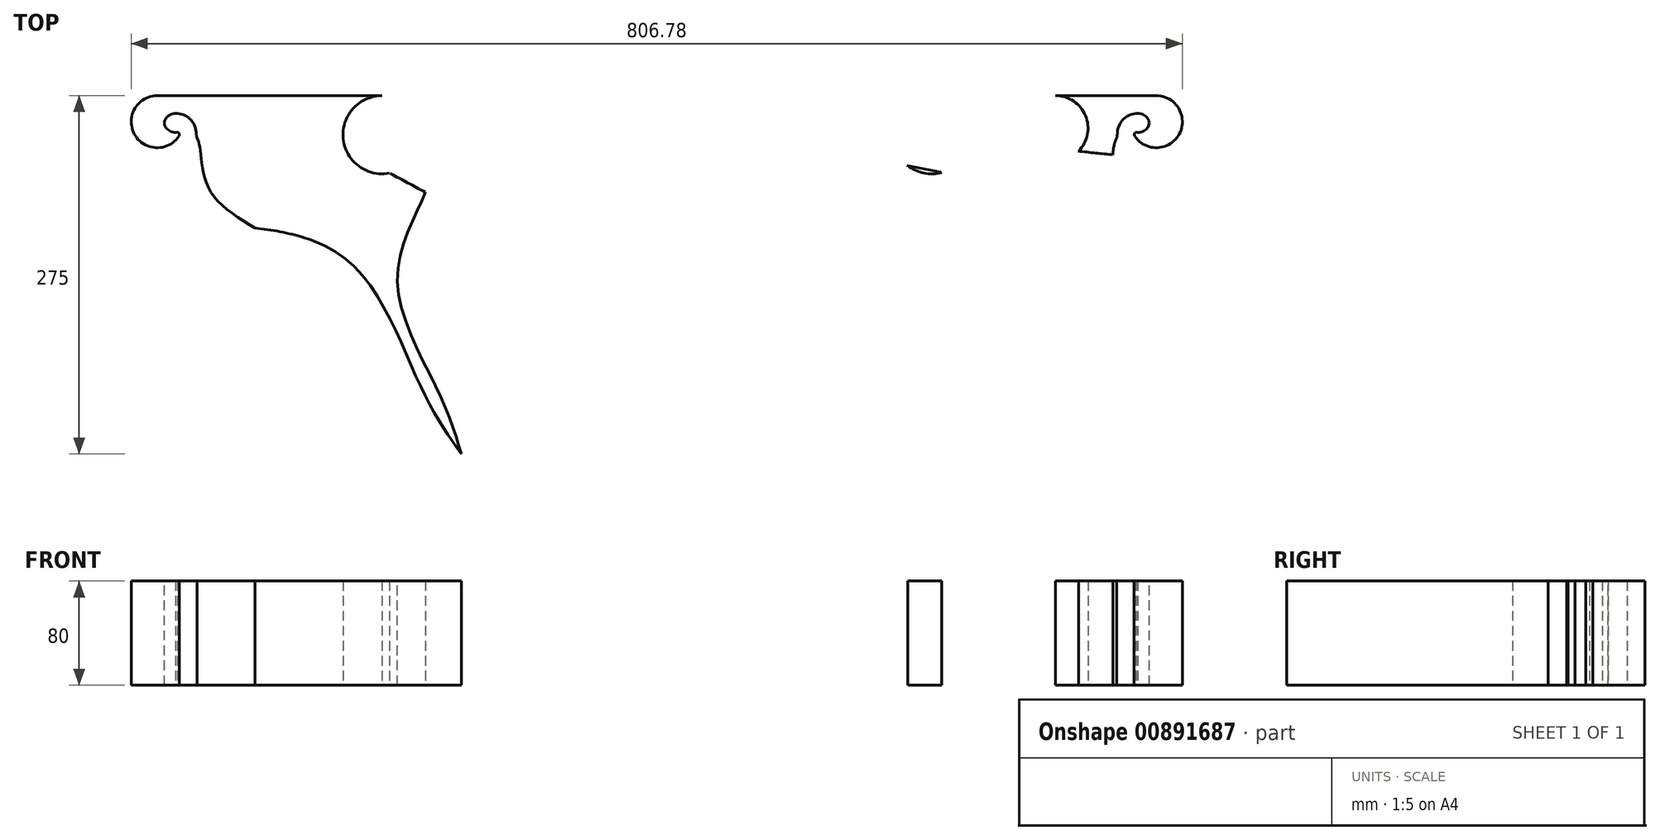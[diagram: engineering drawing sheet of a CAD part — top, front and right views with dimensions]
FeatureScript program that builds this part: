
annotation { "Feature Type Name" : "Feature", "Feature Type Description" : "" }
export const myFeature = defineFeature(function(context is Context, id is Id, definition is map)
    precondition{}
    {
        {
            var Q0;
            Q0=qCreatedBy(makeId("Top.planeOp"),FACE);
            var sketch = newSketch(context, id + "F0", { "sketchPlane" : qUnion([Q0])});
            skFitSpline(sketch, "E0.0.0", {"points": [v(222.24, 427.22) * mm, v(215.5, 429.07) * mm, v(196.44, 434.28) * mm, v(159.63, 464.69) * mm, v(135.76, 484.28) * mm]});
            skArc(sketch, "E0.0.1", {"start": v(135.76, 484.28) * mm, "mid": v(0, 567.46) * mm, "end": v(-135.76, 484.28) * mm});
            skFitSpline(sketch, "E0.0.2", {"points": [v(-135.76, 484.28) * mm, v(-159.63, 464.69) * mm, v(-196.44, 434.28) * mm, v(-215.5, 429.07) * mm, v(-222.24, 427.22) * mm]});
            skArc(sketch, "E0.0.4", {"start": v(-309.42, 390.28) * mm, "mid": v(-312.68, 382.2) * mm, "end": v(-319.87, 377.3) * mm});
            skFitSpline(sketch, "E0.0.5", {"points": [v(-314.05, 379.09) * mm, v(-349.26, 368.46) * mm, v(-392.1, 351.55) * mm, v(-410.06, 337.43) * mm]});
            skEllipticalArc(sketch, "E0.0.6", {});
            skArc(sketch, "E0.0.7", {"start": v(-404.46, 196.44) * mm, "mid": v(-395.87, 191.21) * mm, "end": v(-386.4, 187.8) * mm});
            skFitSpline(sketch, "E0.0.8", {"points": [v(-394.78, 189.9) * mm, v(-344.92, 177.5) * mm, v(-241.75, 151.88) * mm, v(-181.26, 51.75) * mm, v(-150, 0) * mm]});
            skLineSegment(sketch, "E0.0.9", {"start": v(-150, 0) * mm, "end": v(-90, 0) * mm});
            skLineSegment(sketch, "E0.0.10", {"start": v(-90, 0) * mm, "end": v(-90, 110) * mm});
            skArc(sketch, "E0.0.11", {"start": v(-90, 110) * mm, "mid": v(0, 200) * mm, "end": v(90, 110) * mm});
            skLineSegment(sketch, "E0.0.12", {"start": v(90, 110) * mm, "end": v(90, 0) * mm});
            skLineSegment(sketch, "E0.0.13", {"start": v(90, 0) * mm, "end": v(150, 0) * mm});
            skFitSpline(sketch, "E0.0.14", {"points": [v(150, 0) * mm, v(181.26, 51.75) * mm, v(241.75, 151.88) * mm, v(344.92, 177.5) * mm, v(394.78, 189.9) * mm]});
            skArc(sketch, "E0.0.15", {"start": v(386.4, 187.8) * mm, "mid": v(395.87, 191.21) * mm, "end": v(404.46, 196.44) * mm});
            skEllipticalArc(sketch, "E0.0.16", {});
            skFitSpline(sketch, "E0.0.17", {"points": [v(410.06, 337.43) * mm, v(392.1, 351.55) * mm, v(349.26, 368.46) * mm, v(314.05, 379.09) * mm]});
            skLineSegment(sketch, "E1.0", {"start": v(-240.1, 290) * mm, "end": v(-178.5, 290) * mm});
            skLineSegment(sketch, "E1.1", {"start": v(-178.5, 290) * mm, "end": v(-178.5, 325.2) * mm});
            skLineSegment(sketch, "E1.2", {"start": v(-178.5, 325.2) * mm, "end": v(-240.1, 325.2) * mm});
            skLineSegment(sketch, "E1.3", {"start": v(-240.1, 290) * mm, "end": v(-240.1, 325.2) * mm});
            skLineSegment(sketch, "E1.4", {"start": v(-250.1, 290) * mm, "end": v(-250.1, 325.2) * mm});
            skLineSegment(sketch, "E1.5", {"start": v(-250.1, 325.2) * mm, "end": v(-311.7, 325.2) * mm});
            skLineSegment(sketch, "E1.6", {"start": v(-311.7, 290) * mm, "end": v(-250.1, 290) * mm});
            skLineSegment(sketch, "E1.7", {"start": v(-311.7, 290) * mm, "end": v(-311.7, 325.2) * mm});
            skLineSegment(sketch, "E2.0", {"start": v(-383.3, 290) * mm, "end": v(-321.7, 290) * mm});
            skLineSegment(sketch, "E3.0", {"start": v(-321.7, 325.2) * mm, "end": v(-383.3, 325.2) * mm});
            skLineSegment(sketch, "E4.0", {"start": v(-321.7, 290) * mm, "end": v(-321.7, 325.2) * mm});
            skLineSegment(sketch, "E5.0", {"start": v(-383.3, 290) * mm, "end": v(-383.3, 325.2) * mm});
            skFitSpline(sketch, "E6.0", {"points": [v(-342.67, 339.28) * mm, v(-317.97, 353.62) * mm, v(-277.69, 364.45) * mm, v(-252.88, 405.7) * mm, v(-252.65, 405.6) * mm, v(-252.66, 408.6) * mm]});
            skArc(sketch, "E7.0", {"start": v(-250.27, 406.87) * mm, "mid": v(-251.77, 407.17) * mm, "end": v(-252.75, 406) * mm});
            skFitSpline(sketch, "E8.0", {"points": [v(-250.27, 406.87) * mm, v(-244.43, 403.08) * mm, v(-228.6, 392.87) * mm, v(-192.33, 407.72) * mm, v(-169.18, 417.08) * mm]});
            skArc(sketch, "E9.0", {"start": v(-169.05, 414.28) * mm, "mid": v(-169.97, 415.86) * mm, "end": v(-171.8, 416.02) * mm});
            skArc(sketch, "E10.0", {"start": v(-332.8, 344.66) * mm, "mid": v(-334, 342.02) * mm, "end": v(-331.71, 340.22) * mm});
            skArc(sketch, "E11.0.0", {"start": v(367.9, 246.89) * mm, "mid": v(366.57, 245.65) * mm, "end": v(366.79, 243.85) * mm});
            skArc(sketch, "E11.0.1", {"start": v(366.79, 243.85) * mm, "mid": v(401.04, 245.6) * mm, "end": v(383.39, 275) * mm});
            skLineSegment(sketch, "E11.0.2", {"start": v(383.39, 275) * mm, "end": v(-383.39, 275) * mm});
            skArc(sketch, "E11.0.3", {"start": v(-383.39, 275) * mm, "mid": v(-401.04, 245.6) * mm, "end": v(-366.79, 243.85) * mm});
            skArc(sketch, "E11.0.4", {"start": v(-366.79, 243.85) * mm, "mid": v(-366.57, 245.65) * mm, "end": v(-367.9, 246.89) * mm});
            skEllipticalArc(sketch, "E11.0.5", {});
            skArc(sketch, "E11.0.6", {"start": v(-369.23, 261.25) * mm, "mid": v(-358.46, 257.25) * mm, "end": v(-353.55, 246.86) * mm});
            skArc(sketch, "E11.0.7", {"start": v(-353.55, 246.86) * mm, "mid": v(-353.08, 242.95) * mm, "end": v(-352.1, 239.13) * mm});
            skFitSpline(sketch, "E11.0.8", {"points": [v(-353.7, 243.85) * mm, v(-350.61, 235.19) * mm, v(-342.3, 200.93) * mm, v(-287.54, 161.27) * mm, v(-255.18, 135.34) * mm]});
            skFitSpline(sketch, "E11.0.9", {"points": [v(-394.78, 189.9) * mm, v(-344.92, 177.5) * mm, v(-241.75, 151.88) * mm, v(-181.26, 51.75) * mm, v(-150, 0) * mm]});
            skFitSpline(sketch, "E11.0.15", {"points": [v(150, 0) * mm, v(181.26, 51.75) * mm, v(241.75, 151.88) * mm, v(344.92, 177.5) * mm, v(394.78, 189.9) * mm]});
            skFitSpline(sketch, "E11.0.16", {"points": [v(255.18, 135.34) * mm, v(287.54, 161.27) * mm, v(342.3, 200.93) * mm, v(350.61, 235.19) * mm, v(353.7, 243.85) * mm]});
            skArc(sketch, "E11.0.17", {"start": v(352.1, 239.13) * mm, "mid": v(353.08, 242.95) * mm, "end": v(353.55, 246.86) * mm});
            skArc(sketch, "E11.0.18", {"start": v(353.55, 246.86) * mm, "mid": v(358.46, 257.25) * mm, "end": v(369.23, 261.25) * mm});
            skEllipticalArc(sketch, "E11.0.19", {});
            skLineSegment(sketch, "E12.0.0", {"start": v(305.94, 275) * mm, "end": v(-305.94, 275) * mm});
            skArc(sketch, "E12.0.1", {"start": v(-305.94, 275) * mm, "mid": v(-327.36, 237.1) * mm, "end": v(-283.84, 238.31) * mm});
            skArc(sketch, "E12.0.2", {"start": v(-283.84, 238.31) * mm, "mid": v(-283.78, 240.06) * mm, "end": v(-285.12, 241.19) * mm});
            skEllipticalArc(sketch, "E12.0.3", {});
            skFitSpline(sketch, "E12.0.4", {"points": [v(-286.27, 259.2) * mm, v(1000, -265.74) * mm, v(256.47, 1000) * mm]});
            skFitSpline(sketch, "E12.0.5", {"points": [v(-285.63, 259.1) * mm, v(1000, -265.14) * mm, v(258.09, 1000) * mm]});
            skFitSpline(sketch, "E12.0.6", {"points": [v(-265.5, 243.26) * mm, v(-263.97, 221.32) * mm, v(-260.75, 173.86) * mm, v(-230.38, 123.02) * mm, v(-214.22, 95.6) * mm]});
            skFitSpline(sketch, "E12.0.7", {"points": [v(-394.78, 189.9) * mm, v(-344.92, 177.5) * mm, v(-241.75, 151.88) * mm, v(-181.26, 51.75) * mm, v(-150, 0) * mm]});
            skFitSpline(sketch, "E12.0.13", {"points": [v(150, 0) * mm, v(181.26, 51.75) * mm, v(241.75, 151.88) * mm, v(344.92, 177.5) * mm, v(394.78, 189.9) * mm]});
            skFitSpline(sketch, "E12.0.14", {"points": [v(214.22, 95.6) * mm, v(230.38, 123.02) * mm, v(260.75, 173.86) * mm, v(263.97, 221.32) * mm, v(265.5, 243.26) * mm]});
            skFitSpline(sketch, "E12.0.15", {"points": [v(265.14, 238.31) * mm, v(1000, 265.14) * mm, v(258.09, 1000) * mm]});
            skLineSegment(sketch, "E12.0.16", {"start": v(285.63, 259.1) * mm, "end": v(286.27, 259.2) * mm});
            skEllipticalArc(sketch, "E12.0.17", {});
            skArc(sketch, "E12.0.18", {"start": v(285.12, 241.19) * mm, "mid": v(283.78, 240.06) * mm, "end": v(283.84, 238.31) * mm});
            skArc(sketch, "E12.0.19", {"start": v(283.84, 238.31) * mm, "mid": v(327.36, 237.1) * mm, "end": v(305.94, 275) * mm});
            skArc(sketch, "E13.0.0", {"start": v(188.69, 224.82) * mm, "mid": v(238.32, 232.86) * mm, "end": v(210.88, 275) * mm});
            skLineSegment(sketch, "E13.0.1", {"start": v(210.88, 275) * mm, "end": v(-210.88, 275) * mm});
            skArc(sketch, "E13.0.2", {"start": v(-210.88, 275) * mm, "mid": v(-238.32, 232.86) * mm, "end": v(-188.69, 224.82) * mm});
            skArc(sketch, "E13.0.3", {"start": v(-188.69, 224.82) * mm, "mid": v(-188.58, 226.71) * mm, "end": v(-190.1, 227.85) * mm});
            skEllipticalArc(sketch, "E13.0.4", {});
            skFitSpline(sketch, "E13.0.5", {"points": [v(-190.78, 251.9) * mm, v(1000, -168.95) * mm, v(251.9, 1000) * mm]});
            skArc(sketch, "E13.0.6", {"start": v(-170.52, 233.6) * mm, "mid": v(-170.48, 227.5) * mm, "end": v(-171.67, 221.5) * mm});
            skFitSpline(sketch, "E13.0.7", {"points": [v(-170.36, 225.76) * mm, v(-179.25, 197.05) * mm, v(-199.12, 132.86) * mm, v(-167.48, 47.3) * mm, v(-150, 0) * mm]});
            skFitSpline(sketch, "E13.0.13", {"points": [v(150, 0) * mm, v(167.48, 47.3) * mm, v(199.12, 132.86) * mm, v(179.25, 197.05) * mm, v(170.36, 225.76) * mm]});
            skArc(sketch, "E13.0.14", {"start": v(171.67, 221.5) * mm, "mid": v(170.48, 227.5) * mm, "end": v(170.52, 233.6) * mm});
            skFitSpline(sketch, "E13.0.15", {"points": [v(170.36, 225.76) * mm, v(1000, 168.95) * mm, v(251.9, 1000) * mm]});
            skEllipticalArc(sketch, "E13.0.16", {});
            skArc(sketch, "E13.0.17", {"start": v(190.1, 227.85) * mm, "mid": v(188.58, 226.71) * mm, "end": v(188.69, 224.82) * mm});
            skLineSegment(sketch, "E14", {"start": v(-331.71, 340.22) * mm, "end": v(-198.5, 340.69) * mm});
            skLineSegment(sketch, "E15", {"start": v(-168.92, 340.79) * mm, "end": v(-169.05, 414.28) * mm});
            skFitSpline(sketch, "E16", {"points": [v(-309.42, 390.28) * mm, v(-310.43, 397.88) * mm, v(-313.22, 403.87) * mm, v(-319.74, 407.36) * mm, v(-326.56, 409.03) * mm, v(-336.27, 408.88) * mm, v(-344.6, 406.3) * mm, v(-349.31, 401.45) * mm, v(-350.68, 396.14) * mm, v(-348.1, 390.38) * mm, v(-342.18, 385.98) * mm, v(-349.31, 386.43) * mm, v(-357.3, 391.91) * mm, v(-359.87, 398.89) * mm, v(-360.53, 404.48) * mm, v(-359.92, 410.03) * mm, v(-358.56, 414.95) * mm, v(-355.53, 420.61) * mm, v(-347.6, 428.48) * mm, v(-336.84, 434.93) * mm, v(-325.35, 437.99) * mm, v(-316.06, 437.95) * mm, v(-306.16, 435.7) * mm, v(-299.83, 432.89) * mm, v(-292.54, 427.4) * mm, v(-289.54, 422.08) * mm, v(-289.78, 416.43) * mm, v(-288.99, 413.5) * mm, v(-284.18, 413.54) * mm, v(-277.28, 420.3) * mm, v(-275.39, 426.5) * mm, v(-275.68, 437.35) * mm, v(-274.73, 450.85) * mm, v(-268.87, 462.58) * mm, v(-258.44, 470.61) * mm, v(-245.92, 473.96) * mm, v(-234.58, 474.32) * mm, v(-224.62, 471.95) * mm, v(-219.05, 468.93) * mm, v(-214.82, 465.41) * mm, v(-210.76, 459.35) * mm, v(-210.3, 450.66) * mm, v(-213.6, 444.23) * mm, v(-219.23, 439.08) * mm, v(-223.94, 437.12) * mm, v(-226.82, 436.48) * mm, v(-228.8, 436.84) * mm, v(-227, 438.29) * mm, v(-224.93, 439.28) * mm, v(-222.76, 440.81) * mm, v(-221.4, 443.17) * mm, v(-220.7, 446.77) * mm, v(-221.12, 450.52) * mm, v(-223.7, 453.85) * mm, v(-227.55, 456.2) * mm, v(-231.66, 457.32) * mm, v(-236.43, 457.82) * mm, v(-239.68, 457.23) * mm, v(-243.44, 455.26) * mm, v(-247.03, 451.54) * mm, v(-248.96, 447.62) * mm, v(-249.62, 441.06) * mm, v(-248.82, 436.85) * mm, v(-246.6, 432.46) * mm, v(-243.05, 429.54) * mm, v(-238.25, 427.74) * mm, v(-231.93, 426.7) * mm, v(-225.96, 426.77) * mm, v(-222.24, 427.22) * mm], "startDerivative": vector(-24.65, 493.31) * mm, "endDerivative": vector(305.63, 42.31) * mm});
            skFitSpline(sketch, "E17.MirrorCS", {"points": [v(309.42, 390.28) * mm, v(310.43, 397.88) * mm, v(313.22, 403.87) * mm, v(319.74, 407.36) * mm, v(326.56, 409.03) * mm, v(336.27, 408.88) * mm, v(344.6, 406.3) * mm, v(349.31, 401.45) * mm, v(350.68, 396.14) * mm, v(348.1, 390.38) * mm, v(342.18, 385.98) * mm, v(349.31, 386.43) * mm, v(357.3, 391.91) * mm, v(359.87, 398.89) * mm, v(360.53, 404.48) * mm, v(359.92, 410.03) * mm, v(358.56, 414.95) * mm, v(355.53, 420.61) * mm, v(347.6, 428.48) * mm, v(336.84, 434.93) * mm, v(325.35, 437.99) * mm, v(316.06, 437.95) * mm, v(306.16, 435.7) * mm, v(299.83, 432.89) * mm, v(292.54, 427.4) * mm, v(289.54, 422.08) * mm, v(289.78, 416.43) * mm, v(288.99, 413.5) * mm, v(284.18, 413.54) * mm, v(277.28, 420.3) * mm, v(275.39, 426.5) * mm, v(275.68, 437.35) * mm, v(274.73, 450.85) * mm, v(268.87, 462.58) * mm, v(258.44, 470.61) * mm, v(245.92, 473.96) * mm, v(234.58, 474.32) * mm, v(224.62, 471.95) * mm, v(219.05, 468.93) * mm, v(214.82, 465.41) * mm, v(210.76, 459.35) * mm, v(210.3, 450.66) * mm, v(213.6, 444.23) * mm, v(219.23, 439.08) * mm, v(223.94, 437.12) * mm, v(226.82, 436.48) * mm, v(228.8, 436.84) * mm, v(227, 438.29) * mm, v(224.93, 439.28) * mm, v(222.76, 440.81) * mm, v(221.4, 443.17) * mm, v(220.7, 446.77) * mm, v(221.12, 450.52) * mm, v(223.7, 453.85) * mm, v(227.55, 456.2) * mm, v(231.66, 457.32) * mm, v(236.43, 457.82) * mm, v(239.68, 457.23) * mm, v(243.44, 455.26) * mm, v(247.03, 451.54) * mm, v(248.96, 447.62) * mm, v(249.62, 441.06) * mm, v(248.82, 436.85) * mm, v(246.6, 432.46) * mm, v(243.05, 429.54) * mm, v(238.25, 427.74) * mm, v(231.93, 426.7) * mm, v(225.96, 426.77) * mm, v(222.24, 427.22) * mm], "startDerivative": vector(24.65, 493.31) * mm, "endDerivative": vector(-305.63, 42.31) * mm});
            skFitSpline(sketch, "E18.MirrorCS", {"points": [v(342.67, 339.28) * mm, v(317.97, 353.62) * mm, v(277.69, 364.45) * mm, v(252.88, 405.7) * mm, v(252.65, 405.6) * mm, v(252.66, 408.6) * mm]});
            skFitSpline(sketch, "E19.MirrorCS", {"points": [v(250.27, 406.87) * mm, v(244.43, 403.08) * mm, v(228.6, 392.87) * mm, v(192.33, 407.72) * mm, v(169.18, 417.08) * mm]});
            skLineSegment(sketch, "E20.MirrorCS", {"start": v(168.92, 340.79) * mm, "end": v(169.05, 414.28) * mm});
            skLineSegment(sketch, "E21.MirrorCS", {"start": v(331.71, 340.22) * mm, "end": v(168.92, 340.79) * mm});
            skArc(sketch, "E22.MirrorCS", {"start": v(169.05, 414.28) * mm, "mid": v(169.97, 415.86) * mm, "end": v(171.8, 416.02) * mm});
            skArc(sketch, "E23.MirrorCS", {"start": v(250.27, 406.87) * mm, "mid": v(251.77, 407.17) * mm, "end": v(252.75, 406) * mm});
            skArc(sketch, "E24.MirrorCS", {"start": v(332.8, 344.66) * mm, "mid": v(334, 342.02) * mm, "end": v(331.71, 340.22) * mm});
            skArc(sketch, "E25.MirrorCS", {"start": v(309.42, 390.28) * mm, "mid": v(312.68, 382.2) * mm, "end": v(319.87, 377.3) * mm});
            skFitSpline(sketch, "E26", {"points": [v(-250.27, 406.87) * mm, v(-244.43, 403.08) * mm, v(-228.6, 392.87) * mm, v(-192.33, 407.72) * mm, v(-169.18, 417.08) * mm]});
            skLineSegment(sketch, "E27", {"start": v(-198.5, 340.69) * mm, "end": v(-168.92, 340.79) * mm});
            skPoint(sketch, "E28", {"position": v(0, 275) * mm});
            skLineSegment(sketch, "E29", {"start": v(-178.5, 340.75) * mm, "end": v(-178.5, 413.32) * mm});
            skLineSegment(sketch, "E30.MirrorCS", {"start": v(178.5, 340.75) * mm, "end": v(178.5, 413.32) * mm});
            skLineSegment(sketch, "E31.MirrorCS", {"start": v(178.5, 290) * mm, "end": v(178.5, 325.2) * mm});
            skLineSegment(sketch, "E32.MirrorCS", {"start": v(178.5, 325.2) * mm, "end": v(240.1, 325.2) * mm});
            skLineSegment(sketch, "E33.MirrorCS", {"start": v(240.1, 290) * mm, "end": v(178.5, 290) * mm});
            skLineSegment(sketch, "E34.MirrorCS", {"start": v(240.1, 290) * mm, "end": v(240.1, 325.2) * mm});
            skLineSegment(sketch, "E35.MirrorCS", {"start": v(250.1, 290) * mm, "end": v(250.1, 325.2) * mm});
            skLineSegment(sketch, "E36.MirrorCS", {"start": v(250.1, 325.2) * mm, "end": v(311.7, 325.2) * mm});
            skLineSegment(sketch, "E37.MirrorCS", {"start": v(311.7, 290) * mm, "end": v(250.1, 290) * mm});
            skLineSegment(sketch, "E38.MirrorCS", {"start": v(311.7, 290) * mm, "end": v(311.7, 325.2) * mm});
            skLineSegment(sketch, "E39.MirrorCS", {"start": v(321.7, 290) * mm, "end": v(321.7, 325.2) * mm});
            skLineSegment(sketch, "E40.MirrorCS", {"start": v(321.7, 325.2) * mm, "end": v(383.3, 325.2) * mm});
            skLineSegment(sketch, "E41.MirrorCS", {"start": v(383.3, 290) * mm, "end": v(321.7, 290) * mm});
            skLineSegment(sketch, "E42.MirrorCS", {"start": v(383.3, 290) * mm, "end": v(383.3, 325.2) * mm});
            const initialGuessF0  = {"E0.0.6": [-0.34931216680627963, 0.26310522471521947, -0.8795186508433591, 0.4758644164241295, 0.09801349999999999, 0.086147, 5.8461119226871325, 1.3987543209554119], "E0.0.16": [0.34931216680627963, 0.26310522471521947, 0.8795186508433591, 0.4758644164241295, 0.09801349999999999, 0.086147, 4.884430986224174, 0.4370733844924535], "E11.0.5": [-0.3692299729374505, 0.25402610760164496, -1, 0, 0.00868, 0.0072229875998473525, 4.71238898038469, 1.7242785659408997], "E11.0.19": [0.3692299729374472, 0.2540261076016343, 1, 0, 0.00868, 0.0072229875998473525, 4.558906741237017, 1.5707963267948966], "E12.0.3": [-0.2862692176634982, 0.25016623719894915, 1, 0, 0.01114790895395411, 0.00902888915716235, 1.5707963267948966, 4.816091749526819], "E12.0.17": [0.28626921761494883, 0.25016623719894915, 1, 0, 0.01114790895395411, 0.00902888915716235, 4.6086862112438105, 1.5707963267948968], "E13.0.4": [-0.19077662931411604, 0.2398668370838165, -1, 0, 0.012873693325351057, 0.012037203490749382, 4.71238898038469, 1.6233236227230905], "E13.0.16": [0.19077662931381673, 0.2398668370838165, -1, 0, 0.012873693325351057, 0.012037203490749382, 1.5182690308667026, 4.71238898038469]};
            skSetInitialGuess(sketch, initialGuessF0);
            skSolve(sketch);
        }
        {
            var Q0;
            Q0=qCreatedBy(makeId("Top.planeOp"),FACE);
            var sketch = newSketch(context, id + "F1", { "sketchPlane" : qUnion([Q0])});
            skArc(sketch, "E43.0.0", {"start": v(119.38, 608.82) * mm, "mid": v(127.8, 607.3) * mm, "end": v(129.32, 598.88) * mm});
            skArc(sketch, "E43.0.1", {"start": v(129.32, 598.88) * mm, "mid": v(127.96, 594.8) * mm, "end": v(127.5, 590.54) * mm});
            skLineSegment(sketch, "E43.0.2", {"start": v(127.5, 590.54) * mm, "end": v(127.5, 457) * mm});
            skFitSpline(sketch, "E43.0.5", {"points": [v(146.5, 457) * mm, v(149.6, 481.12) * mm, v(148.09, 514.33) * mm, v(141.97, 555.55) * mm, v(150.87, 577.14) * mm, v(150.08, 584.83) * mm, v(149.2, 590.04) * mm, v(146.76, 595.97) * mm, v(148.7, 602.44) * mm, v(153.43, 607.82) * mm, v(159.2, 620.23) * mm, v(152.22, 634.34) * mm, v(138.51, 640.38) * mm, v(127.66, 637.82) * mm, v(123.75, 632.76) * mm, v(115.5, 631.57) * mm, v(101.19, 632.87) * mm, v(83.98, 643.25) * mm, v(68.12, 650.61) * mm, v(57.61, 655.2) * mm, v(46.5, 657.99) * mm, v(38.39, 655.17) * mm, v(34.33, 652.95) * mm, v(28.58, 651.08) * mm, v(24.82, 655.4) * mm, v(15.24, 664.25) * mm, v(0, 668.44) * mm, v(-15.24, 664.25) * mm, v(-24.82, 655.4) * mm, v(-28.58, 651.08) * mm, v(-34.33, 652.95) * mm, v(-38.39, 655.17) * mm, v(-46.5, 657.99) * mm, v(-57.61, 655.2) * mm, v(-68.12, 650.61) * mm, v(-83.98, 643.25) * mm, v(-101.19, 632.87) * mm, v(-115.5, 631.57) * mm, v(-123.75, 632.76) * mm, v(-127.66, 637.82) * mm, v(-138.51, 640.38) * mm, v(-152.22, 634.34) * mm, v(-159.2, 620.23) * mm, v(-153.43, 607.82) * mm, v(-148.7, 602.44) * mm, v(-146.76, 595.97) * mm, v(-149.2, 590.04) * mm, v(-150.08, 584.83) * mm, v(-150.87, 577.14) * mm, v(-141.97, 555.55) * mm, v(-148.09, 514.33) * mm, v(-149.6, 481.12) * mm, v(-146.5, 457) * mm]});
            skLineSegment(sketch, "E43.0.8", {"start": v(-127.5, 457) * mm, "end": v(-127.5, 590.54) * mm});
            skArc(sketch, "E43.0.9", {"start": v(-127.5, 590.54) * mm, "mid": v(-127.96, 594.8) * mm, "end": v(-129.32, 598.88) * mm});
            skArc(sketch, "E43.0.10", {"start": v(-129.32, 598.88) * mm, "mid": v(-127.8, 607.3) * mm, "end": v(-119.38, 608.82) * mm});
            skArc(sketch, "E43.0.11", {"start": v(-119.38, 608.82) * mm, "mid": v(-115.3, 607.46) * mm, "end": v(-111.04, 607) * mm});
            skLineSegment(sketch, "E43.0.12", {"start": v(-111.04, 607) * mm, "end": v(111.04, 607) * mm});
            skArc(sketch, "E43.0.13", {"start": v(111.04, 607) * mm, "mid": v(115.3, 607.46) * mm, "end": v(119.38, 608.82) * mm});
            skLineSegment(sketch, "E44.0.0", {"start": v(117.5, 597) * mm, "end": v(117.5, 457) * mm});
            skLineSegment(sketch, "E44.0.2", {"start": v(127.5, 457) * mm, "end": v(127.5, 596.4) * mm});
            skArc(sketch, "E44.0.3", {"start": v(127.5, 596.4) * mm, "mid": v(127.8, 607.3) * mm, "end": v(116.9, 607) * mm});
            skLineSegment(sketch, "E44.0.4", {"start": v(116.9, 607) * mm, "end": v(-116.9, 607) * mm});
            skArc(sketch, "E44.0.5", {"start": v(-116.9, 607) * mm, "mid": v(-127.8, 607.3) * mm, "end": v(-127.5, 596.4) * mm});
            skLineSegment(sketch, "E44.0.6", {"start": v(-127.5, 596.4) * mm, "end": v(-127.5, 457) * mm});
            skLineSegment(sketch, "E44.0.8", {"start": v(-117.5, 457) * mm, "end": v(-117.5, 597) * mm});
            skLineSegment(sketch, "E44.0.9", {"start": v(-117.5, 597) * mm, "end": v(117.5, 597) * mm});
            skLineSegment(sketch, "E45.0.0", {"start": v(107.5, 587) * mm, "end": v(107.5, 457) * mm});
            skLineSegment(sketch, "E45.0.2", {"start": v(117.5, 457) * mm, "end": v(117.5, 597) * mm});
            skLineSegment(sketch, "E45.0.3", {"start": v(117.5, 597) * mm, "end": v(-117.5, 597) * mm});
            skLineSegment(sketch, "E45.0.4", {"start": v(-117.5, 597) * mm, "end": v(-117.5, 457) * mm});
            skLineSegment(sketch, "E45.0.6", {"start": v(-107.5, 457) * mm, "end": v(-107.5, 587) * mm});
            skLineSegment(sketch, "E45.0.7", {"start": v(-107.5, 587) * mm, "end": v(107.5, 587) * mm});
            skLineSegment(sketch, "E46", {"start": v(-146.5, 457) * mm, "end": v(146.5, 457) * mm});
            skPoint(sketch, "E43.0.3.end.orphan", {"position": v(146.5, 447) * mm});
            skPoint(sketch, "E47.orphan", {"position": v(117.5, 447) * mm});
            skPoint(sketch, "E48.orphan", {"position": v(127.5, 447) * mm});
            skPoint(sketch, "E49.orphan", {"position": v(107.5, 447) * mm});
            skPoint(sketch, "E50.orphan", {"position": v(-117.5, 447) * mm});
            skPoint(sketch, "E43.0.7.end.orphan", {"position": v(-127.5, 447) * mm});
            skArc(sketch, "E51.MirrorCS", {"start": v(129.32, 315.12) * mm, "mid": v(127.96, 319.2) * mm, "end": v(127.5, 323.46) * mm});
            skArc(sketch, "E52.MirrorCS", {"start": v(111.04, 307) * mm, "mid": v(115.3, 306.54) * mm, "end": v(119.38, 305.18) * mm});
            skArc(sketch, "E53.MirrorCS", {"start": v(127.5, 317.6) * mm, "mid": v(127.8, 306.7) * mm, "end": v(116.9, 307) * mm});
            skArc(sketch, "E54.MirrorCS", {"start": v(-116.9, 307) * mm, "mid": v(-127.8, 306.7) * mm, "end": v(-127.5, 317.6) * mm});
            skArc(sketch, "E55.MirrorCS", {"start": v(119.38, 305.18) * mm, "mid": v(127.8, 306.7) * mm, "end": v(129.32, 315.12) * mm});
            skArc(sketch, "E56.MirrorCS", {"start": v(-119.38, 305.18) * mm, "mid": v(-115.3, 306.54) * mm, "end": v(-111.04, 307) * mm});
            skArc(sketch, "E57.MirrorCS", {"start": v(-129.32, 315.12) * mm, "mid": v(-127.8, 306.7) * mm, "end": v(-119.38, 305.18) * mm});
            skArc(sketch, "E58.MirrorCS", {"start": v(-127.5, 323.46) * mm, "mid": v(-127.96, 319.2) * mm, "end": v(-129.32, 315.12) * mm});
            skLineSegment(sketch, "E59.MirrorCS", {"start": v(127.5, 323.46) * mm, "end": v(127.5, 457) * mm});
            skLineSegment(sketch, "E60.MirrorCS", {"start": v(-111.04, 307) * mm, "end": v(111.04, 307) * mm});
            skPoint(sketch, "E61.MirrorP", {"position": v(117.5, 467) * mm});
            skLineSegment(sketch, "E62.MirrorCS", {"start": v(-127.5, 457) * mm, "end": v(-127.5, 323.46) * mm});
            skLineSegment(sketch, "E63.MirrorCS", {"start": v(-117.5, 317) * mm, "end": v(-117.5, 457) * mm});
            skLineSegment(sketch, "E64.MirrorCS", {"start": v(117.5, 317) * mm, "end": v(-117.5, 317) * mm});
            skPoint(sketch, "E65.MirrorP", {"position": v(127.5, 467) * mm});
            skLineSegment(sketch, "E66.MirrorCS", {"start": v(117.5, 457) * mm, "end": v(117.5, 317) * mm});
            skPoint(sketch, "E67.MirrorP", {"position": v(107.5, 467) * mm});
            skPoint(sketch, "E68.MirrorP", {"position": v(146.5, 467) * mm});
            skLineSegment(sketch, "E69.MirrorCS", {"start": v(-107.5, 327) * mm, "end": v(107.5, 327) * mm});
            skPoint(sketch, "E70.MirrorP", {"position": v(-117.5, 467) * mm});
            skLineSegment(sketch, "E71.MirrorCS", {"start": v(127.5, 457) * mm, "end": v(127.5, 317.6) * mm});
            skPoint(sketch, "E72.MirrorP", {"position": v(-127.5, 467) * mm});
            skLineSegment(sketch, "E73.MirrorCS", {"start": v(-117.5, 457) * mm, "end": v(-117.5, 317) * mm});
            skLineSegment(sketch, "E74.MirrorCS", {"start": v(107.5, 327) * mm, "end": v(107.5, 457) * mm});
            skLineSegment(sketch, "E75.MirrorCS", {"start": v(-127.5, 317.6) * mm, "end": v(-127.5, 457) * mm});
            skLineSegment(sketch, "E76.MirrorCS", {"start": v(-107.5, 457) * mm, "end": v(-107.5, 327) * mm});
            skFitSpline(sketch, "E77.MirrorCS", {"points": [v(146.5, 457) * mm, v(149.6, 432.88) * mm, v(148.09, 399.67) * mm, v(141.97, 358.45) * mm, v(150.87, 336.86) * mm, v(150.08, 329.17) * mm, v(149.2, 323.96) * mm, v(146.76, 318.03) * mm, v(148.7, 311.56) * mm, v(153.43, 306.18) * mm, v(159.2, 293.77) * mm, v(152.22, 279.66) * mm, v(138.51, 273.62) * mm, v(127.66, 276.18) * mm, v(123.75, 281.24) * mm, v(115.5, 282.43) * mm, v(101.19, 281.13) * mm, v(83.98, 270.75) * mm, v(68.12, 263.39) * mm, v(57.61, 258.8) * mm, v(46.5, 256.01) * mm, v(38.39, 258.83) * mm, v(34.33, 261.05) * mm, v(28.58, 262.92) * mm, v(24.82, 258.6) * mm, v(15.24, 249.75) * mm, v(0, 245.56) * mm, v(-15.24, 249.75) * mm, v(-24.82, 258.6) * mm, v(-28.58, 262.92) * mm, v(-34.33, 261.05) * mm, v(-38.39, 258.83) * mm, v(-46.5, 256.01) * mm, v(-57.61, 258.8) * mm, v(-68.12, 263.39) * mm, v(-83.98, 270.75) * mm, v(-101.19, 281.13) * mm, v(-115.5, 282.43) * mm, v(-123.75, 281.24) * mm, v(-127.66, 276.18) * mm, v(-138.51, 273.62) * mm, v(-152.22, 279.66) * mm, v(-159.2, 293.77) * mm, v(-153.43, 306.18) * mm, v(-148.7, 311.56) * mm, v(-146.76, 318.03) * mm, v(-149.2, 323.96) * mm, v(-150.08, 329.17) * mm, v(-150.87, 336.86) * mm, v(-141.97, 358.45) * mm, v(-148.09, 399.67) * mm, v(-149.6, 432.88) * mm, v(-146.5, 457) * mm]});
            skLineSegment(sketch, "E78.MirrorCS", {"start": v(116.9, 307) * mm, "end": v(-116.9, 307) * mm});
            skLineSegment(sketch, "E79.MirrorCS", {"start": v(117.5, 317) * mm, "end": v(117.5, 457) * mm});
            skLineSegment(sketch, "E80.MirrorCS", {"start": v(-117.5, 317) * mm, "end": v(117.5, 317) * mm});
            skLineSegment(sketch, "E81.0", {"start": v(-138, 275) * mm, "end": v(138, 275) * mm});
            skFitSpline(sketch, "E82.trimOffspring", {"points": [v(146.5, 457) * mm, v(149.6, 432.88) * mm, v(148.09, 399.67) * mm, v(141.97, 358.45) * mm, v(150.87, 336.86) * mm, v(150.08, 329.17) * mm, v(149.2, 323.96) * mm, v(146.76, 318.03) * mm, v(148.7, 311.56) * mm, v(153.43, 306.18) * mm, v(159.2, 293.77) * mm, v(152.22, 279.66) * mm, v(138.51, 273.62) * mm, v(127.66, 276.18) * mm, v(123.75, 281.24) * mm, v(115.5, 282.43) * mm, v(101.19, 281.13) * mm, v(83.98, 270.75) * mm, v(68.12, 263.39) * mm, v(57.61, 258.8) * mm, v(46.5, 256.01) * mm, v(38.39, 258.83) * mm, v(34.33, 261.05) * mm, v(28.58, 262.92) * mm, v(24.82, 258.6) * mm, v(15.24, 249.75) * mm, v(0, 245.56) * mm, v(-15.24, 249.75) * mm, v(-24.82, 258.6) * mm, v(-28.58, 262.92) * mm, v(-34.33, 261.05) * mm, v(-38.39, 258.83) * mm, v(-46.5, 256.01) * mm, v(-57.61, 258.8) * mm, v(-68.12, 263.39) * mm, v(-83.98, 270.75) * mm, v(-101.19, 281.13) * mm, v(-115.5, 282.43) * mm, v(-123.75, 281.24) * mm, v(-127.66, 276.18) * mm, v(-138.51, 273.62) * mm, v(-152.22, 279.66) * mm, v(-159.2, 293.77) * mm, v(-153.43, 306.18) * mm, v(-148.7, 311.56) * mm, v(-146.76, 318.03) * mm, v(-149.2, 323.96) * mm, v(-150.08, 329.17) * mm, v(-150.87, 336.86) * mm, v(-141.97, 358.45) * mm, v(-148.09, 399.67) * mm, v(-149.6, 432.88) * mm, v(-146.5, 457) * mm]});
            skPoint(sketch, "E83", {"position": v(0, 275) * mm});
            skPoint(sketch, "E84", {"position": v(0, 667) * mm});
            skSolve(sketch);
        }
        {
            var Q0;
            Q0=makeQuery(id+"F0.imprint","IMPRINT",FACE,{"disambiguationData":[TD([[makeQuery(id+"F0.imprint","IMPRINT",EDGE,{"derivedFrom":sQuery(id+"F0.wireOp",EDGE,"E0.0.0")}),1.0]])]});
            var Q1;
            {var subQ1=sQuery(id+"F0.wireOp",EDGE,"E11.0.3");Q1=makeQuery(id+"F0.imprint","IMPRINT",FACE,{"disambiguationData":[TD([[makeQuery(id+"F0.imprint","IMPRINT",EDGE,{"derivedFrom":subQ1}),1.0]])]});}
            var Q2;
            {var subQ1=sQuery(id+"F0.wireOp",EDGE,"E12.0.1");Q2=makeQuery(id+"F0.imprint","IMPRINT",FACE,{"disambiguationData":[TD([[makeQuery(id+"F0.imprint","IMPRINT",EDGE,{"derivedFrom":subQ1}),1.0]])]});}
            var Q3;
            Q3=makeQuery(id+"F0.imprint","IMPRINT",FACE,{"disambiguationData":[TD([[makeQuery(id+"F0.imprint","IMPRINT",EDGE,{"derivedFrom":sQuery(id+"F0.wireOp",EDGE,"E13.0.0")}),1.0]])]});
            var Q4;
            Q4=makeQuery(id+"F0.imprint","IMPRINT",FACE,{"disambiguationData":[TD([[makeQuery(id+"F0.imprint","IMPRINT",EDGE,{"derivedFrom":sQuery(id+"F0.wireOp",EDGE,"E12.0.13")}),1.0]])]});
            var Q5;
            Q5=makeQuery(id+"F0.imprint","IMPRINT",FACE,{"disambiguationData":[TD([[makeQuery(id+"F0.imprint","IMPRINT",EDGE,{"derivedFrom":sQuery(id+"F0.wireOp",EDGE,"E11.0.0")}),1.0]])]});
            var Q6;
            {var subQ4=sQuery(id+"F0.wireOp",EDGE,"E9.0");Q6=makeQuery(id+"F0.imprint","IMPRINT",FACE,{"disambiguationData":[TD([[makeQuery(id+"F0.imprint","IMPRINT",EDGE,{"derivedFrom":subQ4}),1.0]])]});}
            var Q7;
            {var subQ2=sQuery(id+"F0.wireOp",EDGE,"E20.MirrorCS");Q7=makeQuery(id+"F0.imprint","IMPRINT",FACE,{"disambiguationData":[TD([[makeQuery(id+"F0.imprint","IMPRINT",EDGE,{"derivedFrom":subQ2}),-1.0]])]});}
            extrude(context, id + "F2", {"entities" : qUnion([Q0, Q1, Q2, Q3, Q4, Q5, Q6, Q7]), "depth" : 80 * mm, "offsetDistance" : 25 * mm});
        }
        {
            var Q0;
            Q0=makeQuery(id+"F2.opExtrude","CAP_FACE",FACE,{"disambiguationData":[OSD([sQuery(id+"F0.wireOp",EDGE,"E0.0.0"),sQuery(id+"F0.wireOp",EDGE,"E0.0.1"),sQuery(id+"F0.wireOp",EDGE,"E0.0.2"),sQuery(id+"F0.wireOp",EDGE,"E0.0.4"),sQuery(id+"F0.wireOp",EDGE,"E0.0.5"),sQuery(id+"F0.wireOp",EDGE,"E0.0.6"),sQuery(id+"F0.wireOp",EDGE,"E0.0.7"),sQuery(id+"F0.wireOp",EDGE,"E0.0.8"),sQuery(id+"F0.wireOp",EDGE,"E0.0.14"),sQuery(id+"F0.wireOp",EDGE,"E0.0.15"),sQuery(id+"F0.wireOp",EDGE,"E0.0.16"),sQuery(id+"F0.wireOp",EDGE,"E0.0.17"),sQuery(id+"F0.wireOp",EDGE,"E1.0"),sQuery(id+"F0.wireOp",EDGE,"E1.1"),sQuery(id+"F0.wireOp",EDGE,"E1.2"),sQuery(id+"F0.wireOp",EDGE,"E1.3"),sQuery(id+"F0.wireOp",EDGE,"E1.4"),sQuery(id+"F0.wireOp",EDGE,"E1.5"),sQuery(id+"F0.wireOp",EDGE,"E1.6"),sQuery(id+"F0.wireOp",EDGE,"E1.7"),sQuery(id+"F0.wireOp",EDGE,"E2.0"),sQuery(id+"F0.wireOp",EDGE,"E3.0"),sQuery(id+"F0.wireOp",EDGE,"E4.0"),sQuery(id+"F0.wireOp",EDGE,"E5.0"),sQuery(id+"F0.wireOp",EDGE,"E6.0"),sQuery(id+"F0.wireOp",EDGE,"E7.0"),sQuery(id+"F0.wireOp",EDGE,"E8.0"),sQuery(id+"F0.wireOp",EDGE,"E10.0"),sQuery(id+"F0.wireOp",EDGE,"E11.0.9"),sQuery(id+"F0.wireOp",EDGE,"E11.0.15"),sQuery(id+"F0.wireOp",EDGE,"E12.0.7"),sQuery(id+"F0.wireOp",EDGE,"E12.0.13"),sQuery(id+"F0.wireOp",EDGE,"E0.0.9"),sQuery(id+"F0.wireOp",EDGE,"E0.0.10"),sQuery(id+"F0.wireOp",EDGE,"E0.0.11"),sQuery(id+"F0.wireOp",EDGE,"E0.0.12"),sQuery(id+"F0.wireOp",EDGE,"E0.0.13"),sQuery(id+"F0.wireOp",EDGE,"E14"),sQuery(id+"F0.wireOp",EDGE,"E16"),sQuery(id+"F0.wireOp",EDGE,"E17.MirrorCS"),sQuery(id+"F0.wireOp",EDGE,"E18.MirrorCS"),sQuery(id+"F0.wireOp",EDGE,"E19.MirrorCS"),sQuery(id+"F0.wireOp",EDGE,"E21.MirrorCS"),sQuery(id+"F0.wireOp",EDGE,"E23.MirrorCS"),sQuery(id+"F0.wireOp",EDGE,"E24.MirrorCS"),sQuery(id+"F0.wireOp",EDGE,"E25.MirrorCS"),sQuery(id+"F0.wireOp",EDGE,"E26"),sQuery(id+"F0.wireOp",EDGE,"E27"),sQuery(id+"F0.wireOp",EDGE,"E29"),sQuery(id+"F0.wireOp",EDGE,"E30.MirrorCS"),sQuery(id+"F0.wireOp",EDGE,"E31.MirrorCS"),sQuery(id+"F0.wireOp",EDGE,"E32.MirrorCS"),sQuery(id+"F0.wireOp",EDGE,"E33.MirrorCS"),sQuery(id+"F0.wireOp",EDGE,"E34.MirrorCS"),sQuery(id+"F0.wireOp",EDGE,"E35.MirrorCS"),sQuery(id+"F0.wireOp",EDGE,"E36.MirrorCS"),sQuery(id+"F0.wireOp",EDGE,"E37.MirrorCS"),sQuery(id+"F0.wireOp",EDGE,"E38.MirrorCS"),sQuery(id+"F0.wireOp",EDGE,"E39.MirrorCS"),sQuery(id+"F0.wireOp",EDGE,"E40.MirrorCS"),sQuery(id+"F0.wireOp",EDGE,"E41.MirrorCS"),sQuery(id+"F0.wireOp",EDGE,"E42.MirrorCS")])],"isStart":false});
            cPlane(context, id + "F3", {"entities" : qUnion([Q0]), "cplaneType" : CPlaneType.OFFSET, "offset" : 50 * mm, "width" : 150 * mm, "height" : 150 * mm});
        }
    });
